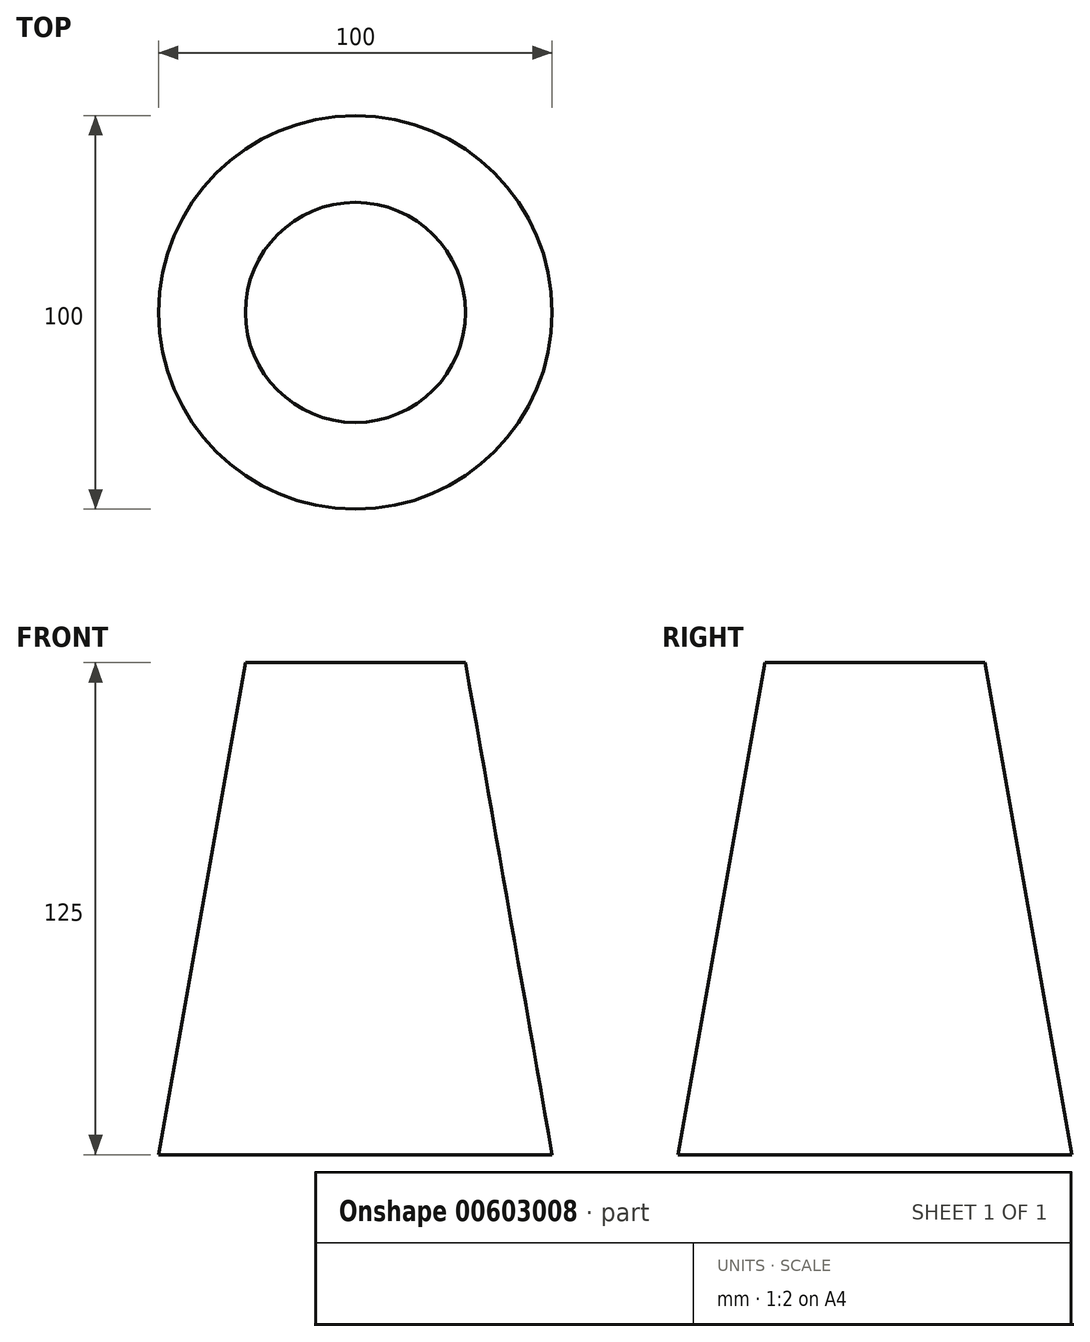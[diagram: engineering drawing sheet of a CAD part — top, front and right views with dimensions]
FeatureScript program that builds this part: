
annotation { "Feature Type Name" : "Feature", "Feature Type Description" : "" }
export const myFeature = defineFeature(function(context is Context, id is Id, definition is map)
    precondition{}
    {
        {
            var Q0;
            Q0=qCreatedBy(makeId("Top.planeOp"),FACE);
            var sketch = newSketch(context, id + "F0", { "sketchPlane" : qUnion([Q0])});
            skCircle(sketch, "E0", {"center": v(0, 0) * mm, "radius": 50 * mm});
            skSolve(sketch);
        }
        {
            var Q0;
            Q0=makeQuery(id+"F0.imprint","IMPRINT",FACE,{"disambiguationData":[TD([[makeQuery(id+"F0.imprint","IMPRINT",EDGE,{"derivedFrom":sQuery(id+"F0.wireOp",EDGE,"E0")}),1.0]])]});
            extrude(context, id + "F1", {"entities" : qUnion([Q0]), "depth" : 125 * mm, "offsetDistance" : 25 * mm, "hasDraft" : true, "draftAngle" : 10 * degree, "draftPullDirection" : true});
        }
    });
